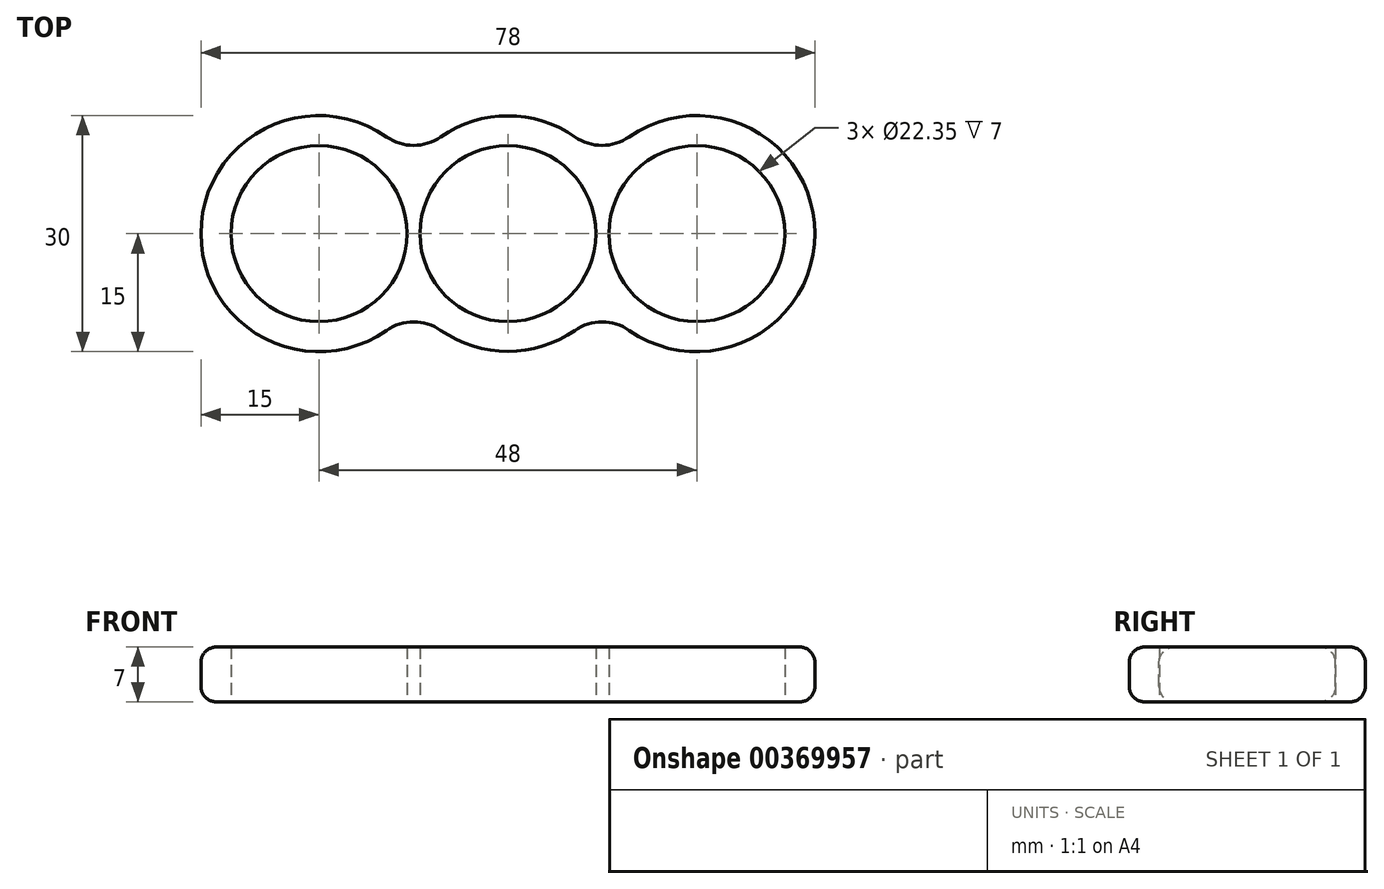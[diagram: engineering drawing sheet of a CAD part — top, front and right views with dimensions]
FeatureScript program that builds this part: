
annotation { "Feature Type Name" : "Feature", "Feature Type Description" : "" }
export const myFeature = defineFeature(function(context is Context, id is Id, definition is map)
    precondition{}
    {
        {
            var Q0;
            Q0=qCreatedBy(makeId("Top.planeOp"),FACE);
            var sketch = newSketch(context, id + "F0", { "sketchPlane" : qUnion([Q0])});
            skCircle(sketch, "E0", {"center": v(0, 0) * mm, "radius": 11.18 * mm});
            skCircle(sketch, "E1", {"center": v(-24, 0) * mm, "radius": 11.18 * mm});
            skCircle(sketch, "E2", {"center": v(24, 0) * mm, "radius": 11.18 * mm});
            skCircle(sketch, "E3", {"center": v(-24, 0) * mm, "radius": 15 * mm});
            skCircle(sketch, "E4", {"center": v(24, 0) * mm, "radius": 15 * mm});
            skCircle(sketch, "E5", {"center": v(0, 0) * mm, "radius": 14.96 * mm});
            skSolve(sketch);
        }
        {
            var Q0;
            Q0=makeQuery(id+"F0.imprint","IMPRINT",FACE,{"disambiguationData":[TD([[makeQuery(id+"F0.imprint","IMPRINT",EDGE,{"derivedFrom":sQuery(id+"F0.wireOp",EDGE,"ffvuShuj-OshO-c5hs-WDAR-ZuKsQZ1vnmAR")}),-1.0]])]});
            var Q1;
            Q1=makeQuery(id+"F0.imprint","IMPRINT",FACE,{"disambiguationData":[TD([[makeQuery(id+"F0.imprint","IMPRINT",EDGE,{"derivedFrom":sQuery(id+"F0.wireOp",EDGE,"bwgdsLH4-RZFz-ohqH-dVLa-YRnHy3qik6SV")}),-1.0]])]});
            var Q2;
            Q2=makeQuery(id+"F0.imprint","IMPRINT",FACE,{"disambiguationData":[TD([[makeQuery(id+"F0.imprint","IMPRINT",EDGE,{"derivedFrom":sQuery(id+"F0.wireOp",EDGE,"TINXS8bJ-a08q-0g3v-jvgb-TxoOEa6wy1WR")}),-1.0]])]});
            var Q3;
            {var subQ0=sQuery(id+"F0.wireOp",EDGE,"9GnjF5dk-10nB-Mq5b-Iskw-ds0yqw7a4ucy");var subQ1=sQuery(id+"F0.wireOp",EDGE,"FzkzEjta-EPXN-Z5uv-5ILG-J4rEEolZ74wE");var subQ2=makeQuery(id+"F0.imprint","INTERSECT",VERTEX,{"disambiguationData":[OD(1.0)],"derivedFrom":[subQ1,subQ0]});Q3=makeQuery(id+"F0.imprint","IMPRINT",FACE,{"disambiguationData":[TD([[makeQuery(id+"F0.imprint","IMPRINT",EDGE,{"disambiguationData":[TD([[subQ2,-1.0]])],"derivedFrom":subQ1}),-1.0]])]});}
            var Q4;
            {var subQ0=sQuery(id+"F0.wireOp",EDGE,"6ec109ea-0f7a-418d-82a9-b200b767a9cb0.MirrorCS");var subQ1=sQuery(id+"F0.wireOp",EDGE,"FzkzEjta-EPXN-Z5uv-5ILG-J4rEEolZ74wE");var subQ2=makeQuery(id+"F0.imprint","INTERSECT",VERTEX,{"disambiguationData":[OD(1.0)],"derivedFrom":[subQ1,subQ0]});Q4=makeQuery(id+"F0.imprint","IMPRINT",FACE,{"disambiguationData":[TD([[makeQuery(id+"F0.imprint","IMPRINT",EDGE,{"disambiguationData":[TD([[subQ2,1.0]])],"derivedFrom":subQ1}),-1.0]])]});}
            var Q5;
            {var subQ0=sQuery(id+"F0.wireOp",EDGE,"99vP87gl-wvMF-NPdc-mqaH-cfolrdlP8JtZ");var subQ1=sQuery(id+"F0.wireOp",EDGE,"FzkzEjta-EPXN-Z5uv-5ILG-J4rEEolZ74wE");var subQ2=makeQuery(id+"F0.imprint","INTERSECT",VERTEX,{"disambiguationData":[OD(1.0)],"derivedFrom":[subQ1,subQ0]});Q5=makeQuery(id+"F0.imprint","IMPRINT",FACE,{"disambiguationData":[TD([[makeQuery(id+"F0.imprint","IMPRINT",EDGE,{"disambiguationData":[TD([[subQ2,1.0]])],"derivedFrom":subQ1}),-1.0]])]});}
            var Q6;
            {var subQ0=sQuery(id+"F0.wireOp",EDGE,"FzkzEjta-EPXN-Z5uv-5ILG-J4rEEolZ74wE");var subQ1=makeQuery(id+"F0.imprint","INTERSECT",VERTEX,{"derivedFrom":[sQuery(id+"F0.wireOp",EDGE,"b2ixpRwv-Uinv-SrGr-89pi-S0W5oyQQp6Q2"),subQ0]});Q6=makeQuery(id+"F0.imprint","IMPRINT",FACE,{"disambiguationData":[TD([[makeQuery(id+"F0.imprint","IMPRINT",EDGE,{"disambiguationData":[TD([[subQ1,1.0]])],"derivedFrom":subQ0}),-1.0]])]});}
            var Q7;
            {var subQ0=sQuery(id+"F0.wireOp",EDGE,"E5");var subQ1=sQuery(id+"F0.wireOp",EDGE,"E1");var subQ2=makeQuery(id+"F0.imprint","INTERSECT",VERTEX,{"disambiguationData":[OD(0.0)],"derivedFrom":[subQ1,subQ0]});Q7=makeQuery(id+"F0.imprint","IMPRINT",FACE,{"disambiguationData":[TD([[makeQuery(id+"F0.imprint","IMPRINT",EDGE,{"disambiguationData":[TD([[subQ2,-1.0]])],"derivedFrom":subQ1}),-1.0]])]});}
            var Q8;
            {var subQ1=sQuery(id+"F0.wireOp",EDGE,"E3");var subQ3=sQuery(id+"F0.wireOp",EDGE,"E0");var subQ4=makeQuery(id+"F0.imprint","INTERSECT",VERTEX,{"disambiguationData":[OD(0.0)],"derivedFrom":[subQ3,subQ1]});Q8=makeQuery(id+"F0.imprint","IMPRINT",FACE,{"disambiguationData":[TD([[makeQuery(id+"F0.imprint","IMPRINT",EDGE,{"disambiguationData":[TD([[subQ4,-1.0]])],"derivedFrom":subQ3}),-1.0]])]});}
            var Q9;
            {var subQ0=sQuery(id+"F0.wireOp",EDGE,"E3");var subQ1=sQuery(id+"F0.wireOp",EDGE,"E0");var subQ2=makeQuery(id+"F0.imprint","INTERSECT",VERTEX,{"disambiguationData":[OD(0.0)],"derivedFrom":[subQ1,subQ0]});Q9=makeQuery(id+"F0.imprint","IMPRINT",FACE,{"disambiguationData":[TD([[makeQuery(id+"F0.imprint","IMPRINT",EDGE,{"disambiguationData":[TD([[subQ2,1.0]])],"derivedFrom":subQ1}),-1.0]])]});}
            var Q10;
            {var subQ1=sQuery(id+"F0.wireOp",EDGE,"E4");var subQ3=sQuery(id+"F0.wireOp",EDGE,"E0");var subQ5=makeQuery(id+"F0.imprint","INTERSECT",VERTEX,{"disambiguationData":[OD(0.0)],"derivedFrom":[subQ3,subQ1]});Q10=makeQuery(id+"F0.imprint","IMPRINT",FACE,{"disambiguationData":[TD([[makeQuery(id+"F0.imprint","IMPRINT",EDGE,{"disambiguationData":[TD([[subQ5,1.0]])],"derivedFrom":subQ3}),-1.0]])]});}
            var Q11;
            {var subQ0=sQuery(id+"F0.wireOp",EDGE,"E5");var subQ1=sQuery(id+"F0.wireOp",EDGE,"E2");var subQ2=makeQuery(id+"F0.imprint","INTERSECT",VERTEX,{"disambiguationData":[OD(0.0)],"derivedFrom":[subQ1,subQ0]});Q11=makeQuery(id+"F0.imprint","IMPRINT",FACE,{"disambiguationData":[TD([[makeQuery(id+"F0.imprint","IMPRINT",EDGE,{"disambiguationData":[TD([[subQ2,1.0]])],"derivedFrom":subQ1}),-1.0]])]});}
            var Q12;
            {var subQ0=sQuery(id+"F0.wireOp",EDGE,"E3");var subQ1=sQuery(id+"F0.wireOp",EDGE,"E0");var subQ2=makeQuery(id+"F0.imprint","INTERSECT",VERTEX,{"disambiguationData":[OD(1.0)],"derivedFrom":[subQ1,subQ0]});Q12=makeQuery(id+"F0.imprint","IMPRINT",FACE,{"disambiguationData":[TD([[makeQuery(id+"F0.imprint","IMPRINT",EDGE,{"disambiguationData":[TD([[subQ2,-1.0]])],"derivedFrom":subQ1}),-1.0]])]});}
            var Q13;
            Q13=makeQuery(id+"F0.imprint","IMPRINT",FACE,{"disambiguationData":[TD([[makeQuery(id+"F0.imprint","IMPRINT",EDGE,{"derivedFrom":sQuery(id+"F0.wireOp",EDGE,"E2")}),-1.0]])]});
            var Q14;
            Q14=makeQuery(id+"F0.imprint","IMPRINT",FACE,{"disambiguationData":[TD([[makeQuery(id+"F0.imprint","IMPRINT",EDGE,{"derivedFrom":sQuery(id+"F0.wireOp",EDGE,"E1")}),-1.0]])]});
            extrude(context, id + "F1", {"entities" : qUnion([Q0, Q1, Q2, Q3, Q4, Q5, Q6, Q7, Q8, Q9, Q10, Q11, Q12, Q13, Q14]), "depth" : 7 * mm, "offsetDistance" : 25 * mm});
        }
        {
            var Q0;
            {var subQ0=sQuery(id+"F0.wireOp",EDGE,"E5");var subQ1=sQuery(id+"F0.wireOp",EDGE,"E3");Q0=makeQuery(id+"F1.opExtrude","SWEPT_EDGE",EDGE,{"disambiguationData":[OSD([subQ1,subQ0]),TDD([makeQuery(id+"F0.imprint","INTERSECT",VERTEX,{"disambiguationData":[OD(1.0)],"derivedFrom":[subQ1,subQ0]})])]});}
            var Q1;
            {var subQ0=sQuery(id+"F0.wireOp",EDGE,"E5");var subQ1=sQuery(id+"F0.wireOp",EDGE,"E4");Q1=makeQuery(id+"F1.opExtrude","SWEPT_EDGE",EDGE,{"disambiguationData":[OSD([subQ1,subQ0]),TDD([makeQuery(id+"F0.imprint","INTERSECT",VERTEX,{"disambiguationData":[OD(1.0)],"derivedFrom":[subQ1,subQ0]})])]});}
            var Q2;
            {var subQ0=sQuery(id+"F0.wireOp",EDGE,"E5");var subQ1=sQuery(id+"F0.wireOp",EDGE,"E4");Q2=makeQuery(id+"F1.opExtrude","SWEPT_EDGE",EDGE,{"disambiguationData":[OSD([subQ1,subQ0]),TDD([makeQuery(id+"F0.imprint","INTERSECT",VERTEX,{"disambiguationData":[OD(0.0)],"derivedFrom":[subQ1,subQ0]})])]});}
            var Q3;
            {var subQ0=sQuery(id+"F0.wireOp",EDGE,"E5");var subQ1=sQuery(id+"F0.wireOp",EDGE,"E3");Q3=makeQuery(id+"F1.opExtrude","SWEPT_EDGE",EDGE,{"disambiguationData":[OSD([subQ1,subQ0]),TDD([makeQuery(id+"F0.imprint","INTERSECT",VERTEX,{"disambiguationData":[OD(0.0)],"derivedFrom":[subQ1,subQ0]})])]});}
            fillet(context, id + "F2", {"entities" : qUnion([Q0, Q1, Q2, Q3]), "radius" : 6 * mm, "tangentPropagation" : true, "allowEdgeOverflow" : false});
        }
        {
            var Q0;
            Q0=makeQuery(id+"F1.opExtrude","CAP_EDGE",EDGE,{"disambiguationData":[OSD([sQuery(id+"F0.wireOp",EDGE,"E3")])],"isStart":false});
            var Q1;
            Q1=makeQuery(id+"F1.opExtrude","CAP_EDGE",EDGE,{"disambiguationData":[OSD([sQuery(id+"F0.wireOp",EDGE,"E3")])],"isStart":true});
            fillet(context, id + "F3", {"entities" : qUnion([Q0, Q1]), "radius" : 2 * mm, "tangentPropagation" : true, "allowEdgeOverflow" : false});
        }
    });
